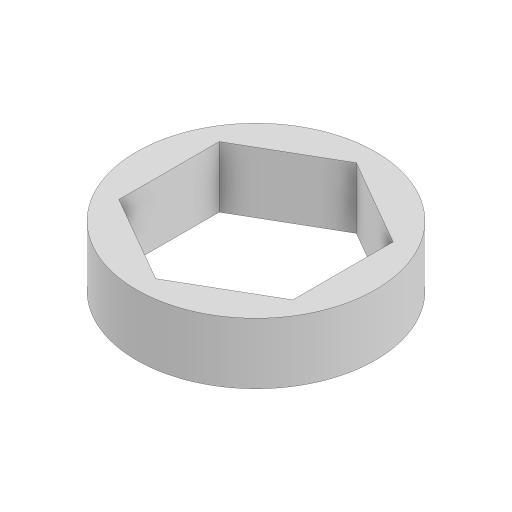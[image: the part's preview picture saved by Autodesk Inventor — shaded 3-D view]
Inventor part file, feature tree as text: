
AUTODESK INVENTOR PART (.ipt)
format: ipt  version: 2024 (Build 280153000, 153)  size: 103,936 bytes
history: native  units: mm
features: extrude x1, sketch x1
ambient origin geometry x8: Origin, YZ Plane, XZ Plane, XY Plane, X Axis, Y Axis, Z Axis, Center Point
bodies: Solid1 (feature_tree)
feature tree (2):
  extrude  "Extrusion1"  Depth=4.6mm
  sketch  "Sketch1"  dims[d0=13.1mm d1=18.0mm d2=4.6mm d3=0.0mm]
